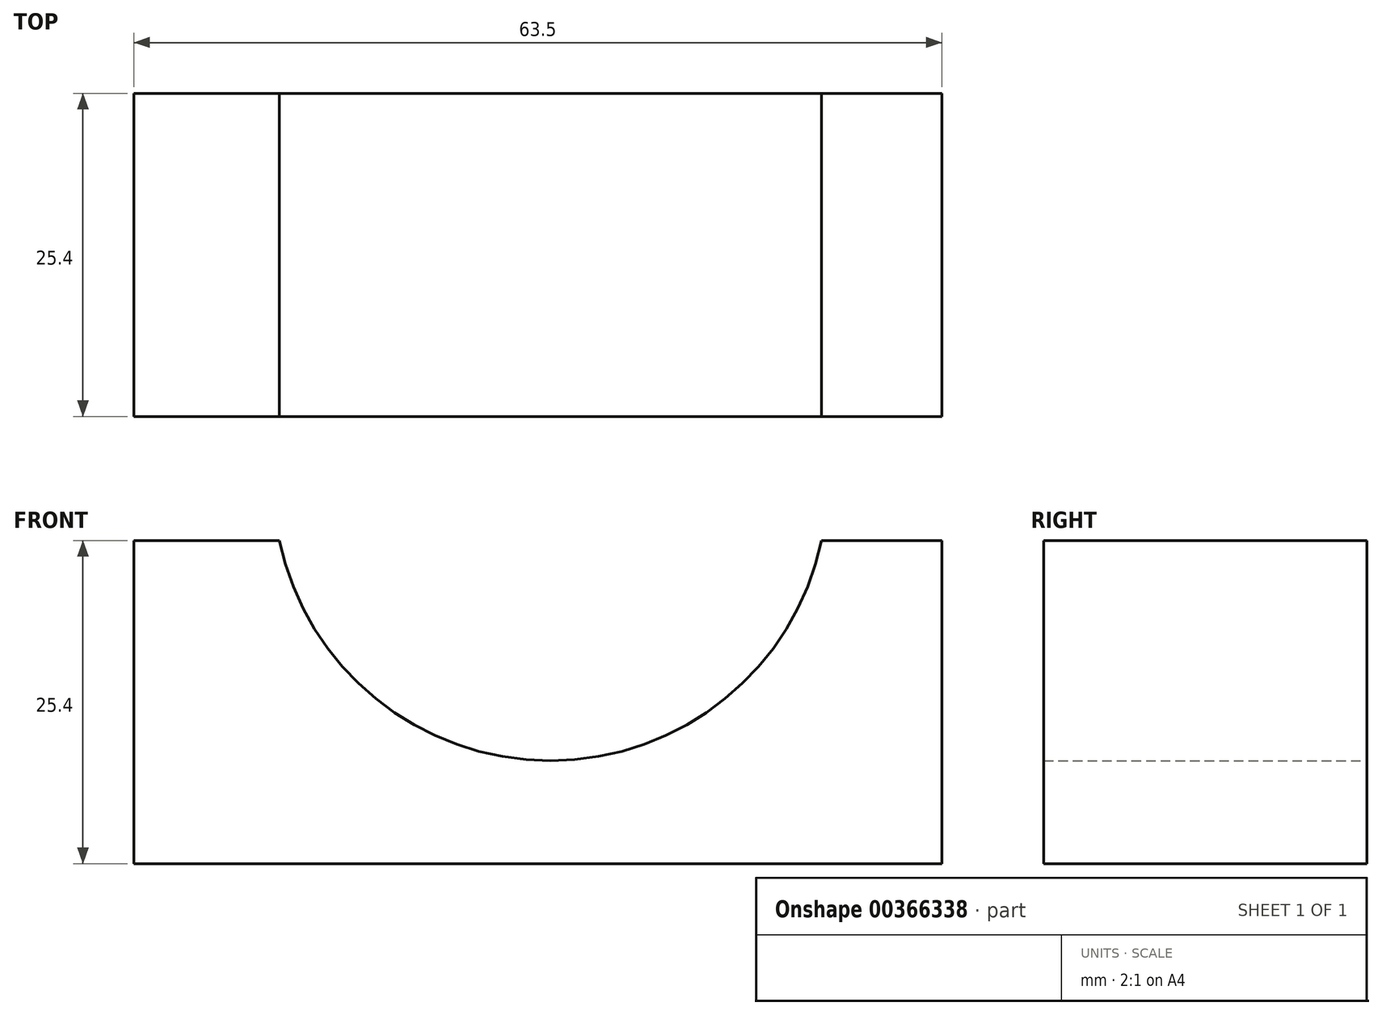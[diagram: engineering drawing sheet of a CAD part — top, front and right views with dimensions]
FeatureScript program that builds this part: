
annotation { "Feature Type Name" : "Feature", "Feature Type Description" : "" }
export const myFeature = defineFeature(function(context is Context, id is Id, definition is map)
    precondition{}
    {
        {
            var Q0;
            Q0=qCreatedBy(makeId("Front.planeOp"),FACE);
            var sketch = newSketch(context, id + "F0", { "sketchPlane" : qUnion([Q0])});
            skLineSegment(sketch, "E0", {"start": v(-34.75, 25.4) * mm, "end": v(-34.75, 0) * mm});
            skLineSegment(sketch, "E1", {"start": v(-34.75, 25.4) * mm, "end": v(28.75, 25.4) * mm});
            skLineSegment(sketch, "E2", {"start": v(28.75, 25.4) * mm, "end": v(28.75, 0) * mm});
            skLineSegment(sketch, "E3", {"start": v(28.75, 0) * mm, "end": v(-34.75, 0) * mm});
            skArc(sketch, "E4", {"start": v(-23.32, 25.4) * mm, "mid": v(-2.01, 8.1) * mm, "end": v(19.3, 25.4) * mm});
            skSolve(sketch);
        }
        {
            var Q0;
            {var subQ3=sQuery(id+"F0.wireOp",EDGE,"E0");Q0=makeQuery(id+"F0.imprint","IMPRINT",FACE,{"disambiguationData":[TD([[makeQuery(id+"F0.imprint","IMPRINT",EDGE,{"derivedFrom":subQ3}),1.0]])]});}
            extrude(context, id + "F1", {"entities" : qUnion([Q0]), "depth" : 25.4 * mm});
        }
    });
